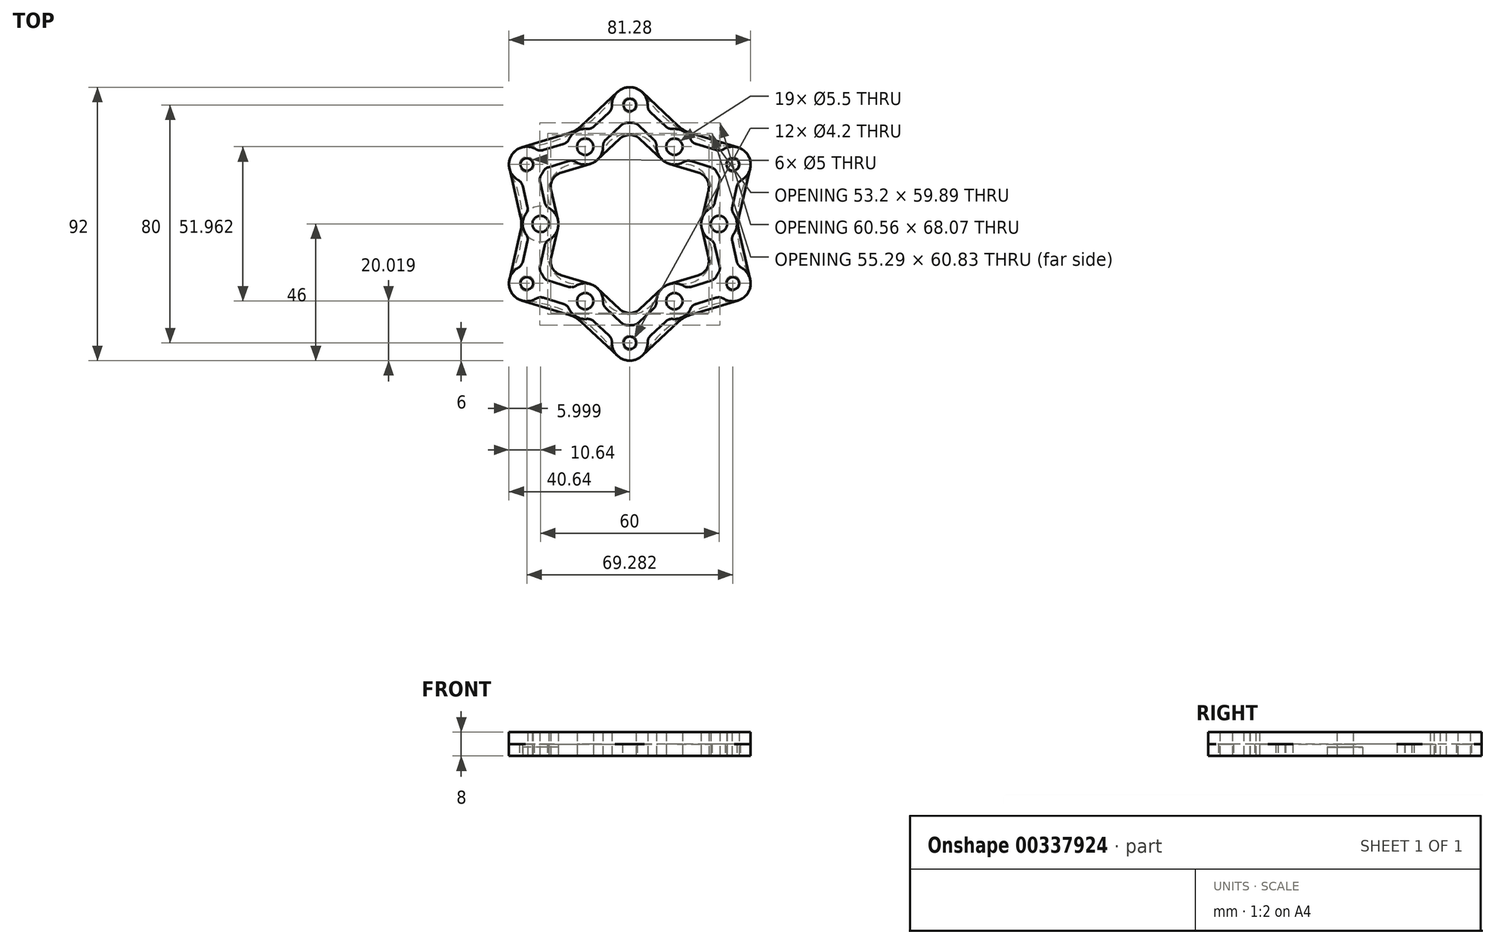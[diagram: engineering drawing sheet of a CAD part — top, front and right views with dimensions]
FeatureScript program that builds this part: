
annotation { "Feature Type Name" : "Feature", "Feature Type Description" : "" }
export const myFeature = defineFeature(function(context is Context, id is Id, definition is map)
    precondition{}
    {
        {
            var Q0;
            Q0=qCreatedBy(makeId("Top.planeOp"),FACE);
            var sketch = newSketch(context, id + "F0", { "sketchPlane" : qUnion([Q0])});
            skLineSegment(sketch, "E0", {"start": v(0, 0) * mm, "end": v(-30, 0) * mm, "construction": true});
            skLineSegment(sketch, "E1", {"start": v(0, 0) * mm, "end": v(-34.64, 20) * mm, "construction": true});
            skLineSegment(sketch, "E2", {"start": v(0, 0) * mm, "end": v(-15, 25.98) * mm, "construction": true});
            skLineSegment(sketch, "E3", {"start": v(-15, 25.98) * mm, "end": v(-12, 20.78) * mm, "construction": true});
            skLineSegment(sketch, "E4", {"start": v(0, 40) * mm, "end": v(0, 0) * mm, "construction": true});
            skCircle(sketch, "E5", {"center": v(-30, 0) * mm, "radius": 2.75 * mm, "construction": true});
            skCircle(sketch, "E6", {"center": v(-34.64, 20) * mm, "radius": 2.5 * mm});
            skCircle(sketch, "E7", {"center": v(-15, 25.98) * mm, "radius": 2.75 * mm});
            skCircle(sketch, "E8", {"center": v(0, 40) * mm, "radius": 2.5 * mm, "construction": true});
            skLineSegment(sketch, "E9", {"start": v(-30, 0) * mm, "end": v(-34.64, 20) * mm, "construction": true});
            skLineSegment(sketch, "E10", {"start": v(-15, 25.98) * mm, "end": v(-34.64, 20) * mm, "construction": true});
            skLineSegment(sketch, "E11", {"start": v(0, 40) * mm, "end": v(-15, 25.98) * mm, "construction": true});
            skArc(sketch, "E12", {"start": v(-35.08, 25.98) * mm, "mid": v(-18.03, 31.23) * mm, "end": v(-4.96, 43.37) * mm});
            skArc(sketch, "E13", {"start": v(-16, 20.07) * mm, "mid": v(-26.34, 15.2) * mm, "end": v(-25.38, 3.83) * mm});
            skLineSegment(sketch, "E14", {"start": v(-34.64, 20) * mm, "end": v(-39.84, 23) * mm, "construction": true});
            skLineSegment(sketch, "E15", {"start": v(0, 40) * mm, "end": v(0, 46) * mm, "construction": true});
            skArc(sketch, "E16", {"start": v(-39.84, 23) * mm, "mid": v(-31.45, 14.92) * mm, "end": v(-35.08, 25.98) * mm, "construction": true});
            skArc(sketch, "E17", {"start": v(-35.08, 25.98) * mm, "mid": v(-37.83, 25.08) * mm, "end": v(-39.84, 23) * mm});
            skLineSegment(sketch, "E18", {"start": v(-12, 20.78) * mm, "end": v(0, 0) * mm, "construction": true});
            skArc(sketch, "E19", {"start": v(-16, 20.07) * mm, "mid": v(-13.94, 20.08) * mm, "end": v(-12, 20.78) * mm});
            skArc(sketch, "E20", {"start": v(-12, 20.78) * mm, "mid": v(-16.06, 31.89) * mm, "end": v(-16, 20.07) * mm, "construction": true});
            skArc(sketch, "E21", {"start": v(-25.38, 3.83) * mm, "mid": v(-35.64, -2.03) * mm, "end": v(-24, 0) * mm, "construction": true});
            skArc(sketch, "E22", {"start": v(-24, 0) * mm, "mid": v(-24.36, 2.03) * mm, "end": v(-25.38, 3.83) * mm});
            skArc(sketch, "E23", {"start": v(-4.96, 43.37) * mm, "mid": v(2.8, 34.7) * mm, "end": v(0, 46) * mm, "construction": true});
            skArc(sketch, "E24", {"start": v(0, 46) * mm, "mid": v(-2.8, 45.3) * mm, "end": v(-4.96, 43.37) * mm});
            skArc(sketch, "E25.1.0", {"start": v(-40.04, -17.4) * mm, "mid": v(-40.64, -20.22) * mm, "end": v(-39.84, -23) * mm});
            skArc(sketch, "E25.1.1", {"start": v(-40.04, -17.4) * mm, "mid": v(-36.07, 0) * mm, "end": v(-40.04, 17.4) * mm});
            skCircle(sketch, "E25.1.2", {"center": v(-34.64, -20) * mm, "radius": 2.5 * mm});
            skCircle(sketch, "E25.1.3", {"center": v(-30, 0) * mm, "radius": 2.75 * mm});
            skArc(sketch, "E25.1.4", {"start": v(-12, -20.78) * mm, "mid": v(-13.94, -20.08) * mm, "end": v(-16, -20.07) * mm});
            skArc(sketch, "E25.1.5", {"start": v(-25.38, -3.83) * mm, "mid": v(-26.34, -15.2) * mm, "end": v(-16, -20.07) * mm});
            skArc(sketch, "E25.1.6", {"start": v(-25.38, -3.83) * mm, "mid": v(-24.36, -2.03) * mm, "end": v(-24, 0) * mm});
            skArc(sketch, "E25.1.7", {"start": v(-39.84, 23) * mm, "mid": v(-40.64, 20.22) * mm, "end": v(-40.04, 17.4) * mm});
            skArc(sketch, "E25.2.0", {"start": v(-4.96, -43.37) * mm, "mid": v(-2.8, -45.3) * mm, "end": v(0, -46) * mm});
            skArc(sketch, "E25.2.1", {"start": v(-4.96, -43.37) * mm, "mid": v(-18.03, -31.23) * mm, "end": v(-35.08, -25.98) * mm});
            skCircle(sketch, "E25.2.2", {"center": v(0, -40) * mm, "radius": 2.5 * mm});
            skCircle(sketch, "E25.2.3", {"center": v(-15, -25.98) * mm, "radius": 2.75 * mm});
            skArc(sketch, "E25.2.4", {"start": v(12, -20.78) * mm, "mid": v(10.42, -22.1) * mm, "end": v(9.37, -23.9) * mm});
            skArc(sketch, "E25.2.5", {"start": v(-9.37, -23.9) * mm, "mid": v(0, -30.41) * mm, "end": v(9.38, -23.9) * mm});
            skArc(sketch, "E25.2.6", {"start": v(-9.37, -23.9) * mm, "mid": v(-10.42, -22.1) * mm, "end": v(-12, -20.78) * mm});
            skArc(sketch, "E25.2.7", {"start": v(-39.84, -23) * mm, "mid": v(-37.83, -25.08) * mm, "end": v(-35.08, -25.98) * mm});
            skArc(sketch, "E25.3.0", {"start": v(35.08, -25.98) * mm, "mid": v(37.83, -25.08) * mm, "end": v(39.84, -23) * mm});
            skArc(sketch, "E25.3.1", {"start": v(35.08, -25.98) * mm, "mid": v(18.03, -31.23) * mm, "end": v(4.96, -43.37) * mm});
            skCircle(sketch, "E25.3.2", {"center": v(34.64, -20) * mm, "radius": 2.5 * mm});
            skCircle(sketch, "E25.3.3", {"center": v(15, -25.98) * mm, "radius": 2.75 * mm});
            skArc(sketch, "E25.3.4", {"start": v(24, 0) * mm, "mid": v(24.36, -2.03) * mm, "end": v(25.38, -3.83) * mm});
            skArc(sketch, "E25.3.5", {"start": v(16, -20.07) * mm, "mid": v(26.34, -15.2) * mm, "end": v(25.38, -3.83) * mm});
            skArc(sketch, "E25.3.6", {"start": v(16, -20.07) * mm, "mid": v(13.94, -20.08) * mm, "end": v(12, -20.78) * mm});
            skArc(sketch, "E25.3.7", {"start": v(0, -46) * mm, "mid": v(2.8, -45.3) * mm, "end": v(4.96, -43.37) * mm});
            skArc(sketch, "E25.4.0", {"start": v(40.04, 17.4) * mm, "mid": v(40.64, 20.22) * mm, "end": v(39.84, 23) * mm});
            skArc(sketch, "E25.4.1", {"start": v(40.04, 17.4) * mm, "mid": v(36.07, 0) * mm, "end": v(40.04, -17.4) * mm});
            skCircle(sketch, "E25.4.2", {"center": v(34.64, 20) * mm, "radius": 2.5 * mm});
            skCircle(sketch, "E25.4.3", {"center": v(30, 0) * mm, "radius": 2.75 * mm});
            skArc(sketch, "E25.4.4", {"start": v(12, 20.78) * mm, "mid": v(13.94, 20.08) * mm, "end": v(16, 20.07) * mm});
            skArc(sketch, "E25.4.5", {"start": v(25.38, 3.83) * mm, "mid": v(26.34, 15.2) * mm, "end": v(16, 20.07) * mm});
            skArc(sketch, "E25.4.6", {"start": v(25.38, 3.83) * mm, "mid": v(24.36, 2.03) * mm, "end": v(24, 0) * mm});
            skArc(sketch, "E25.4.7", {"start": v(39.84, -23) * mm, "mid": v(40.64, -20.22) * mm, "end": v(40.04, -17.4) * mm});
            skArc(sketch, "E25.5.0", {"start": v(4.96, 43.37) * mm, "mid": v(2.8, 45.3) * mm, "end": v(0, 46) * mm});
            skArc(sketch, "E25.5.1", {"start": v(4.96, 43.37) * mm, "mid": v(18.03, 31.23) * mm, "end": v(35.08, 25.98) * mm});
            skCircle(sketch, "E25.5.2", {"center": v(0, 40) * mm, "radius": 2.5 * mm});
            skCircle(sketch, "E25.5.3", {"center": v(15, 25.98) * mm, "radius": 2.75 * mm});
            skArc(sketch, "E25.5.4", {"start": v(-12, 20.78) * mm, "mid": v(-10.42, 22.1) * mm, "end": v(-9.38, 23.9) * mm});
            skArc(sketch, "E25.5.5", {"start": v(9.37, 23.9) * mm, "mid": v(0, 30.41) * mm, "end": v(-9.38, 23.9) * mm});
            skArc(sketch, "E25.5.6", {"start": v(9.37, 23.9) * mm, "mid": v(10.42, 22.1) * mm, "end": v(12, 20.78) * mm});
            skArc(sketch, "E25.5.7", {"start": v(39.84, 23) * mm, "mid": v(37.83, 25.08) * mm, "end": v(35.08, 25.98) * mm});
            skPoint(sketch, "E25.center", {"position": v(0, 0) * mm});
            skSolve(sketch);
        }
        {
            var Q0;
            Q0=makeQuery(id+"F0.imprint","IMPRINT",FACE,{"disambiguationData":[TD([[makeQuery(id+"F0.imprint","IMPRINT",EDGE,{"derivedFrom":sQuery(id+"F0.wireOp",EDGE,"E6")}),-1.0]])]});
            extrude(context, id + "F1", {"entities" : qUnion([Q0]), "depth" : 4 * mm});
        }
        {
            var Q0;
            Q0=qCreatedBy(makeId("Top.planeOp"),FACE);
            var sketch = newSketch(context, id + "F2", { "sketchPlane" : qUnion([Q0])});
            skCircle(sketch, "E26", {"center": v(-30, 0) * mm, "radius": 2.75 * mm});
            skCircle(sketch, "E27", {"center": v(-30, 0) * mm, "radius": 6 * mm});
            skSolve(sketch);
        }
        {
            var Q0;
            Q0 = qSketchRegion(id + "F2", true);
            extrude(context, id + "F3", {"entities" : qUnion([Q0]), "depth" : 3 * mm});
        }
        {
            var Q0;
            Q0=qCreatedBy(makeId("Top.planeOp"),FACE);
            var sketch = newSketch(context, id + "F4", { "sketchPlane" : qUnion([Q0])});
            skCircle(sketch, "E28", {"center": v(-30, 0) * mm, "radius": 2.75 * mm, "construction": true});
            skCircle(sketch, "E29", {"center": v(-34.64, 20) * mm, "radius": 2.1 * mm});
            skCircle(sketch, "E30", {"center": v(-15, 25.98) * mm, "radius": 2.75 * mm});
            skCircle(sketch, "E31", {"center": v(0, 40) * mm, "radius": 2.1 * mm, "construction": true});
            skLineSegment(sketch, "E32", {"start": v(-34.64, 20) * mm, "end": v(0, 0) * mm, "construction": true});
            skLineSegment(sketch, "E33", {"start": v(0, 0) * mm, "end": v(-15, 25.98) * mm, "construction": true});
            skLineSegment(sketch, "E34", {"start": v(-30, 0) * mm, "end": v(0, 0) * mm, "construction": true});
            skLineSegment(sketch, "E35", {"start": v(0, 40) * mm, "end": v(0, 0) * mm, "construction": true});
            skCircle(sketch, "E36", {"center": v(-30, 0) * mm, "radius": 6 * mm, "construction": true});
            skCircle(sketch, "E37", {"center": v(0, 40) * mm, "radius": 6 * mm, "construction": true});
            skLineSegment(sketch, "E38", {"start": v(-30, 0) * mm, "end": v(-34.64, 20) * mm, "construction": true});
            skLineSegment(sketch, "E39", {"start": v(-15, 25.98) * mm, "end": v(-34.64, 20) * mm, "construction": true});
            skLineSegment(sketch, "E40", {"start": v(0, 40) * mm, "end": v(-15, 25.98) * mm, "construction": true});
            skLineSegment(sketch, "E41", {"start": v(-35.84, -1.36) * mm, "end": v(-40.49, 18.64) * mm, "construction": true});
            skLineSegment(sketch, "E42", {"start": v(-36.39, 25.74) * mm, "end": v(-36.39, 25.74) * mm});
            skLineSegment(sketch, "E43", {"start": v(4.1, 35.62) * mm, "end": v(-10.9, 21.6) * mm, "construction": true});
            skLineSegment(sketch, "E44", {"start": v(-13.25, 20.24) * mm, "end": v(-23.06, 17.25) * mm});
            skLineSegment(sketch, "E45", {"start": v(-24.16, 1.36) * mm, "end": v(-26.47, 11.34) * mm});
            skLineSegment(sketch, "E46", {"start": v(-4.1, 44.38) * mm, "end": v(-16.38, 32.9) * mm});
            skLineSegment(sketch, "E47", {"start": v(-36.39, 25.74) * mm, "end": v(-20.3, 30.64) * mm});
            skLineSegment(sketch, "E48", {"start": v(-40.49, 18.64) * mm, "end": v(-40.49, 18.64) * mm});
            skArc(sketch, "E49", {"start": v(-28.8, 21.36) * mm, "mid": v(-31.64, 25.2) * mm, "end": v(-36.39, 25.74) * mm, "construction": true});
            skArc(sketch, "E50", {"start": v(-36.39, 25.74) * mm, "mid": v(-39.84, 23) * mm, "end": v(-40.49, 18.64) * mm});
            skArc(sketch, "E51", {"start": v(-32.9, 14.26) * mm, "mid": v(-29.44, 17) * mm, "end": v(-28.8, 21.36) * mm, "construction": true});
            skArc(sketch, "E52", {"start": v(-40.49, 18.64) * mm, "mid": v(-37.64, 14.8) * mm, "end": v(-32.9, 14.26) * mm, "construction": true});
            skLineSegment(sketch, "E53", {"start": v(-27.53, 15.9) * mm, "end": v(-28.8, 21.36) * mm, "construction": true});
            skLineSegment(sketch, "E54", {"start": v(-27.53, 15.9) * mm, "end": v(-32.9, 14.26) * mm, "construction": true});
            skArc(sketch, "E55", {"start": v(-13.25, 20.24) * mm, "mid": v(-12, 20.78) * mm, "end": v(-10.9, 21.6) * mm});
            skArc(sketch, "E56", {"start": v(-10.9, 21.6) * mm, "mid": v(-18, 31.18) * mm, "end": v(-13.25, 20.24) * mm, "construction": true});
            skLineSegment(sketch, "E57", {"start": v(-18.08, 31.31) * mm, "end": v(-16.75, 31.72) * mm, "construction": true});
            skLineSegment(sketch, "E58", {"start": v(-18.08, 31.31) * mm, "end": v(-19.1, 30.36) * mm, "construction": true});
            skPoint(sketch, "E59.visualSharp", {"position": v(-18.08, 31.31) * mm});
            skArc(sketch, "E59.filletArc", {"start": v(-20.3, 30.64) * mm, "mid": v(-18.21, 31.55) * mm, "end": v(-16.38, 32.9) * mm});
            skPoint(sketch, "E60.visualSharp", {"position": v(-27.53, 15.9) * mm});
            skArc(sketch, "E60.filletArc", {"start": v(-23.06, 17.25) * mm, "mid": v(-25.93, 14.97) * mm, "end": v(-26.47, 11.34) * mm});
            skArc(sketch, "E61.1.0", {"start": v(-40.49, -18.64) * mm, "mid": v(-39.84, -23) * mm, "end": v(-36.39, -25.74) * mm});
            skLineSegment(sketch, "E61.1.1", {"start": v(-40.49, -18.64) * mm, "end": v(-36.68, -2.26) * mm});
            skArc(sketch, "E61.1.2", {"start": v(-36.68, -2.26) * mm, "mid": v(-36.43, 0) * mm, "end": v(-36.68, 2.26) * mm});
            skLineSegment(sketch, "E61.1.3", {"start": v(-40.49, 18.64) * mm, "end": v(-36.68, 2.26) * mm});
            skArc(sketch, "E61.1.4", {"start": v(-24.16, -1.36) * mm, "mid": v(-24, 0) * mm, "end": v(-24.16, 1.36) * mm});
            skLineSegment(sketch, "E61.1.5", {"start": v(-24.16, -1.36) * mm, "end": v(-26.47, -11.34) * mm});
            skArc(sketch, "E61.1.6", {"start": v(-26.47, -11.34) * mm, "mid": v(-25.93, -14.97) * mm, "end": v(-23.06, -17.25) * mm});
            skLineSegment(sketch, "E61.1.7", {"start": v(-13.25, -20.24) * mm, "end": v(-23.06, -17.25) * mm});
            skArc(sketch, "E61.2.0", {"start": v(-4.1, -44.38) * mm, "mid": v(0, -46) * mm, "end": v(4.1, -44.38) * mm});
            skLineSegment(sketch, "E61.2.1", {"start": v(-4.1, -44.38) * mm, "end": v(-16.38, -32.9) * mm});
            skArc(sketch, "E61.2.2", {"start": v(-16.38, -32.9) * mm, "mid": v(-18.21, -31.55) * mm, "end": v(-20.3, -30.64) * mm});
            skLineSegment(sketch, "E61.2.3", {"start": v(-36.39, -25.74) * mm, "end": v(-20.3, -30.64) * mm});
            skArc(sketch, "E61.2.4", {"start": v(-10.9, -21.6) * mm, "mid": v(-12, -20.78) * mm, "end": v(-13.25, -20.24) * mm});
            skLineSegment(sketch, "E61.2.5", {"start": v(-10.9, -21.6) * mm, "end": v(-3.41, -28.6) * mm});
            skArc(sketch, "E61.2.6", {"start": v(-3.41, -28.6) * mm, "mid": v(0, -29.94) * mm, "end": v(3.41, -28.6) * mm});
            skLineSegment(sketch, "E61.2.7", {"start": v(10.9, -21.6) * mm, "end": v(3.41, -28.6) * mm});
            skArc(sketch, "E61.3.0", {"start": v(36.39, -25.74) * mm, "mid": v(39.84, -23) * mm, "end": v(40.49, -18.64) * mm});
            skLineSegment(sketch, "E61.3.1", {"start": v(36.39, -25.74) * mm, "end": v(20.3, -30.64) * mm});
            skArc(sketch, "E61.3.2", {"start": v(20.3, -30.64) * mm, "mid": v(18.21, -31.55) * mm, "end": v(16.38, -32.9) * mm});
            skLineSegment(sketch, "E61.3.3", {"start": v(4.1, -44.38) * mm, "end": v(16.38, -32.9) * mm});
            skArc(sketch, "E61.3.4", {"start": v(13.25, -20.24) * mm, "mid": v(12, -20.78) * mm, "end": v(10.9, -21.6) * mm});
            skLineSegment(sketch, "E61.3.5", {"start": v(13.25, -20.24) * mm, "end": v(23.06, -17.25) * mm});
            skArc(sketch, "E61.3.6", {"start": v(23.06, -17.25) * mm, "mid": v(25.93, -14.97) * mm, "end": v(26.47, -11.34) * mm});
            skLineSegment(sketch, "E61.3.7", {"start": v(24.16, -1.36) * mm, "end": v(26.47, -11.34) * mm});
            skArc(sketch, "E61.4.0", {"start": v(40.49, 18.64) * mm, "mid": v(39.84, 23) * mm, "end": v(36.39, 25.74) * mm});
            skLineSegment(sketch, "E61.4.1", {"start": v(40.49, 18.64) * mm, "end": v(36.68, 2.26) * mm});
            skArc(sketch, "E61.4.2", {"start": v(36.68, 2.26) * mm, "mid": v(36.43, 0) * mm, "end": v(36.68, -2.26) * mm});
            skLineSegment(sketch, "E61.4.3", {"start": v(40.49, -18.64) * mm, "end": v(36.68, -2.26) * mm});
            skArc(sketch, "E61.4.4", {"start": v(24.16, 1.36) * mm, "mid": v(24, 0) * mm, "end": v(24.16, -1.36) * mm});
            skLineSegment(sketch, "E61.4.5", {"start": v(24.16, 1.36) * mm, "end": v(26.47, 11.34) * mm});
            skArc(sketch, "E61.4.6", {"start": v(26.47, 11.34) * mm, "mid": v(25.93, 14.97) * mm, "end": v(23.06, 17.25) * mm});
            skLineSegment(sketch, "E61.4.7", {"start": v(13.25, 20.24) * mm, "end": v(23.06, 17.25) * mm});
            skArc(sketch, "E61.5.0", {"start": v(4.1, 44.38) * mm, "mid": v(0, 46) * mm, "end": v(-4.1, 44.38) * mm});
            skLineSegment(sketch, "E61.5.1", {"start": v(4.1, 44.38) * mm, "end": v(16.38, 32.9) * mm});
            skArc(sketch, "E61.5.2", {"start": v(16.38, 32.9) * mm, "mid": v(18.21, 31.55) * mm, "end": v(20.3, 30.64) * mm});
            skLineSegment(sketch, "E61.5.3", {"start": v(36.39, 25.74) * mm, "end": v(20.3, 30.64) * mm});
            skArc(sketch, "E61.5.4", {"start": v(10.9, 21.6) * mm, "mid": v(12, 20.78) * mm, "end": v(13.25, 20.24) * mm});
            skLineSegment(sketch, "E61.5.5", {"start": v(10.9, 21.6) * mm, "end": v(3.41, 28.6) * mm});
            skArc(sketch, "E61.5.6", {"start": v(3.41, 28.6) * mm, "mid": v(0, 29.94) * mm, "end": v(-3.41, 28.6) * mm});
            skLineSegment(sketch, "E61.5.7", {"start": v(-10.9, 21.6) * mm, "end": v(-3.41, 28.6) * mm});
            skPoint(sketch, "E61.center", {"position": v(0, 0) * mm});
            skCircle(sketch, "E62.1.0", {"center": v(-34.64, -20) * mm, "radius": 2.1 * mm});
            skCircle(sketch, "E62.1.1", {"center": v(-30, 0) * mm, "radius": 2.75 * mm});
            skCircle(sketch, "E62.2.0", {"center": v(0, -40) * mm, "radius": 2.1 * mm});
            skCircle(sketch, "E62.2.1", {"center": v(-15, -25.98) * mm, "radius": 2.75 * mm});
            skCircle(sketch, "E62.3.0", {"center": v(34.64, -20) * mm, "radius": 2.1 * mm});
            skCircle(sketch, "E62.3.1", {"center": v(15, -25.98) * mm, "radius": 2.75 * mm});
            skCircle(sketch, "E62.4.0", {"center": v(34.64, 20) * mm, "radius": 2.1 * mm});
            skCircle(sketch, "E62.4.1", {"center": v(30, 0) * mm, "radius": 2.75 * mm});
            skCircle(sketch, "E62.5.0", {"center": v(0, 40) * mm, "radius": 2.1 * mm});
            skCircle(sketch, "E62.5.1", {"center": v(15, 25.98) * mm, "radius": 2.75 * mm});
            skSolve(sketch);
        }
        {
            var Q0;
            Q0=makeQuery(id+"F4.imprint","IMPRINT",FACE,{"disambiguationData":[TD([[makeQuery(id+"F4.imprint","IMPRINT",EDGE,{"derivedFrom":sQuery(id+"F4.wireOp",EDGE,"E29")}),-1.0]])]});
            extrude(context, id + "F5", {"entities" : qUnion([Q0]), "depth" : 8 * mm});
        }
        {
            var Q0;
            Q0=qCreatedBy(makeId("Top.planeOp"),FACE);
            var sketch = newSketch(context, id + "F6", { "sketchPlane" : qUnion([Q0])});
            skLineSegment(sketch, "E63", {"start": v(-30, 0) * mm, "end": v(0, 0) * mm, "construction": true});
            skLineSegment(sketch, "E64", {"start": v(0, 0) * mm, "end": v(-34.64, 20) * mm, "construction": true});
            skLineSegment(sketch, "E65", {"start": v(-15, 25.98) * mm, "end": v(0, 0) * mm, "construction": true});
            skLineSegment(sketch, "E66", {"start": v(0, 40) * mm, "end": v(0, 0) * mm, "construction": true});
            skCircle(sketch, "E67", {"center": v(-30, 0) * mm, "radius": 2.75 * mm, "construction": true});
            skCircle(sketch, "E68", {"center": v(-15, 25.98) * mm, "radius": 2.75 * mm});
            skCircle(sketch, "E69", {"center": v(-34.64, 20) * mm, "radius": 2.1 * mm});
            skCircle(sketch, "E70", {"center": v(0, 40) * mm, "radius": 2.1 * mm, "construction": true});
            skLineSegment(sketch, "E71", {"start": v(-34.64, 20) * mm, "end": v(-30, 0) * mm, "construction": true});
            skLineSegment(sketch, "E72", {"start": v(-34.64, 20) * mm, "end": v(-15, 25.98) * mm, "construction": true});
            skLineSegment(sketch, "E73", {"start": v(0, 40) * mm, "end": v(-15, 25.98) * mm, "construction": true});
            skLineSegment(sketch, "E74", {"start": v(-6.95, 37.61) * mm, "end": v(-12.15, 32.75) * mm});
            skLineSegment(sketch, "E75", {"start": v(-36.05, 12.79) * mm, "end": v(-34.1, 4.38) * mm, "construction": true});
            skLineSegment(sketch, "E76", {"start": v(-28.25, 5.74) * mm, "end": v(-30.2, 14.14) * mm, "construction": true});
            skLineSegment(sketch, "E77", {"start": v(-27.35, 19.08) * mm, "end": v(-20.54, 21.16) * mm});
            skLineSegment(sketch, "E78", {"start": v(-8.05, 28.37) * mm, "end": v(-2.85, 33.23) * mm});
            skLineSegment(sketch, "E79", {"start": v(-29.1, 24.82) * mm, "end": v(-22.3, 26.9) * mm});
            skArc(sketch, "E80", {"start": v(-36.39, 14.26) * mm, "mid": v(-33.28, 14.16) * mm, "end": v(-30.54, 15.62) * mm, "construction": true});
            skArc(sketch, "E81", {"start": v(-31.53, 25.13) * mm, "mid": v(-39.84, 23) * mm, "end": v(-37.53, 14.74) * mm});
            skArc(sketch, "E82", {"start": v(-28.8, 18.64) * mm, "mid": v(-28.9, 21.75) * mm, "end": v(-30.54, 24.38) * mm, "construction": true});
            skArc(sketch, "E83", {"start": v(-29.73, 16.55) * mm, "mid": v(-29.44, 17) * mm, "end": v(-29.2, 17.48) * mm});
            skArc(sketch, "E84", {"start": v(-20.84, 27.34) * mm, "mid": v(-20.74, 24.23) * mm, "end": v(-19.1, 21.6) * mm, "construction": true});
            skArc(sketch, "E85", {"start": v(-14.46, 31.96) * mm, "mid": v(-18, 31.18) * mm, "end": v(-20.44, 28.5) * mm});
            skArc(sketch, "E86", {"start": v(-9.16, 27.34) * mm, "mid": v(-10.62, 30.08) * mm, "end": v(-13.25, 31.72) * mm, "construction": true});
            skArc(sketch, "E87", {"start": v(-18.11, 20.85) * mm, "mid": v(-12, 20.78) * mm, "end": v(-9, 26.11) * mm});
            skArc(sketch, "E88", {"start": v(-5.84, 38.64) * mm, "mid": v(-4.38, 35.9) * mm, "end": v(-1.75, 34.26) * mm, "construction": true});
            skArc(sketch, "E89", {"start": v(-0.54, 34.02) * mm, "mid": v(4.38, 44.1) * mm, "end": v(-6, 39.87) * mm, "construction": true});
            skArc(sketch, "E90", {"start": v(-34.1, 4.38) * mm, "mid": v(-28.64, -5.84) * mm, "end": v(-28.25, 5.74) * mm, "construction": true});
            skArc(sketch, "E91", {"start": v(-28.25, 5.74) * mm, "mid": v(-31.36, 5.84) * mm, "end": v(-34.1, 4.38) * mm, "construction": true});
            skPoint(sketch, "E92.visualSharp", {"position": v(-36.39, 14.26) * mm});
            skArc(sketch, "E92.filletArc", {"start": v(-36.05, 12.79) * mm, "mid": v(-36.58, 13.92) * mm, "end": v(-37.53, 14.74) * mm, "construction": true});
            skPoint(sketch, "E93.visualSharp", {"position": v(-30.54, 24.38) * mm});
            skArc(sketch, "E93.filletArc", {"start": v(-31.53, 25.13) * mm, "mid": v(-30.35, 24.72) * mm, "end": v(-29.1, 24.82) * mm});
            skPoint(sketch, "E94.visualSharp", {"position": v(-20.84, 27.34) * mm});
            skArc(sketch, "E94.filletArc", {"start": v(-22.3, 26.9) * mm, "mid": v(-21.2, 27.5) * mm, "end": v(-20.44, 28.5) * mm});
            skPoint(sketch, "E95.visualSharp", {"position": v(-13.25, 31.72) * mm});
            skArc(sketch, "E95.filletArc", {"start": v(-14.46, 31.96) * mm, "mid": v(-13.22, 32.1) * mm, "end": v(-12.15, 32.75) * mm});
            skPoint(sketch, "E96.visualSharp", {"position": v(-5.84, 38.64) * mm});
            skArc(sketch, "E96.filletArc", {"start": v(-6.95, 37.61) * mm, "mid": v(-6.23, 38.64) * mm, "end": v(-6, 39.87) * mm});
            skPoint(sketch, "E97.visualSharp", {"position": v(-1.75, 34.26) * mm});
            skArc(sketch, "E97.filletArc", {"start": v(-0.54, 34.02) * mm, "mid": v(-1.78, 33.87) * mm, "end": v(-2.85, 33.23) * mm});
            skPoint(sketch, "E98.visualSharp", {"position": v(-9.16, 27.34) * mm});
            skArc(sketch, "E98.filletArc", {"start": v(-8.05, 28.37) * mm, "mid": v(-8.77, 27.34) * mm, "end": v(-9, 26.11) * mm});
            skPoint(sketch, "E99.visualSharp", {"position": v(-19.1, 21.6) * mm});
            skArc(sketch, "E99.filletArc", {"start": v(-18.11, 20.85) * mm, "mid": v(-19.3, 21.26) * mm, "end": v(-20.54, 21.16) * mm});
            skPoint(sketch, "E100.visualSharp", {"position": v(-28.8, 18.64) * mm});
            skArc(sketch, "E100.filletArc", {"start": v(-27.35, 19.08) * mm, "mid": v(-28.45, 18.48) * mm, "end": v(-29.2, 17.48) * mm});
            skPoint(sketch, "E101.visualSharp", {"position": v(-30.54, 15.62) * mm});
            skArc(sketch, "E101.filletArc", {"start": v(-29.73, 16.55) * mm, "mid": v(-30.22, 15.4) * mm, "end": v(-30.2, 14.14) * mm, "construction": true});
            skArc(sketch, "E102.1.0", {"start": v(-29.2, -17.48) * mm, "mid": v(-29.44, -17) * mm, "end": v(-29.73, -16.55) * mm});
            skArc(sketch, "E102.1.1", {"start": v(-30.2, -14.14) * mm, "mid": v(-30.22, -15.4) * mm, "end": v(-29.73, -16.55) * mm});
            skLineSegment(sketch, "E102.1.2", {"start": v(-30.2, -14.14) * mm, "end": v(-28.6, -7.21) * mm});
            skArc(sketch, "E102.1.3", {"start": v(-27.11, -5.26) * mm, "mid": v(-28.06, -6.08) * mm, "end": v(-28.6, -7.21) * mm});
            skArc(sketch, "E102.1.4", {"start": v(-27.11, -5.26) * mm, "mid": v(-24, 0) * mm, "end": v(-27.11, 5.26) * mm});
            skArc(sketch, "E102.1.5", {"start": v(-28.6, 7.21) * mm, "mid": v(-28.06, 6.08) * mm, "end": v(-27.11, 5.26) * mm});
            skLineSegment(sketch, "E102.1.6", {"start": v(-28.6, 7.21) * mm, "end": v(-30.2, 14.14) * mm});
            skArc(sketch, "E102.1.7", {"start": v(-29.73, 16.55) * mm, "mid": v(-30.22, 15.4) * mm, "end": v(-30.2, 14.14) * mm});
            skArc(sketch, "E102.1.8", {"start": v(-36.05, 12.79) * mm, "mid": v(-36.58, 13.92) * mm, "end": v(-37.53, 14.74) * mm});
            skLineSegment(sketch, "E102.1.9", {"start": v(-36.05, 12.79) * mm, "end": v(-34.44, 5.86) * mm});
            skArc(sketch, "E102.1.10", {"start": v(-34.9, 3.45) * mm, "mid": v(-34.42, 4.6) * mm, "end": v(-34.44, 5.86) * mm});
            skArc(sketch, "E102.1.11", {"start": v(-34.9, 3.45) * mm, "mid": v(-36, 0) * mm, "end": v(-34.9, -3.45) * mm});
            skArc(sketch, "E102.1.12", {"start": v(-34.44, -5.86) * mm, "mid": v(-34.42, -4.6) * mm, "end": v(-34.9, -3.45) * mm});
            skLineSegment(sketch, "E102.1.13", {"start": v(-36.05, -12.79) * mm, "end": v(-34.44, -5.86) * mm});
            skArc(sketch, "E102.1.14", {"start": v(-37.53, -14.74) * mm, "mid": v(-36.58, -13.92) * mm, "end": v(-36.05, -12.79) * mm});
            skArc(sketch, "E102.1.15", {"start": v(-37.53, -14.74) * mm, "mid": v(-39.84, -23) * mm, "end": v(-31.53, -25.13) * mm});
            skCircle(sketch, "E102.1.16", {"center": v(-34.64, -20) * mm, "radius": 2.1 * mm});
            skCircle(sketch, "E102.1.17", {"center": v(-30, 0) * mm, "radius": 2.75 * mm});
            skArc(sketch, "E102.2.0", {"start": v(0.54, -34.02) * mm, "mid": v(0, -34) * mm, "end": v(-0.54, -34.02) * mm});
            skArc(sketch, "E102.2.1", {"start": v(-2.85, -33.23) * mm, "mid": v(-1.78, -33.87) * mm, "end": v(-0.54, -34.02) * mm});
            skLineSegment(sketch, "E102.2.2", {"start": v(-2.85, -33.23) * mm, "end": v(-8.05, -28.37) * mm});
            skArc(sketch, "E102.2.3", {"start": v(-9, -26.11) * mm, "mid": v(-8.77, -27.34) * mm, "end": v(-8.05, -28.37) * mm});
            skArc(sketch, "E102.2.4", {"start": v(-9, -26.11) * mm, "mid": v(-12, -20.78) * mm, "end": v(-18.11, -20.85) * mm});
            skArc(sketch, "E102.2.5", {"start": v(-20.54, -21.16) * mm, "mid": v(-19.3, -21.26) * mm, "end": v(-18.11, -20.85) * mm});
            skLineSegment(sketch, "E102.2.6", {"start": v(-20.54, -21.16) * mm, "end": v(-27.35, -19.08) * mm});
            skArc(sketch, "E102.2.7", {"start": v(-29.2, -17.48) * mm, "mid": v(-28.45, -18.48) * mm, "end": v(-27.35, -19.08) * mm});
            skArc(sketch, "E102.2.8", {"start": v(-29.1, -24.82) * mm, "mid": v(-30.35, -24.72) * mm, "end": v(-31.53, -25.13) * mm});
            skLineSegment(sketch, "E102.2.9", {"start": v(-29.1, -24.82) * mm, "end": v(-22.3, -26.9) * mm});
            skArc(sketch, "E102.2.10", {"start": v(-20.44, -28.5) * mm, "mid": v(-21.2, -27.5) * mm, "end": v(-22.3, -26.9) * mm});
            skArc(sketch, "E102.2.11", {"start": v(-20.44, -28.5) * mm, "mid": v(-18, -31.18) * mm, "end": v(-14.46, -31.96) * mm});
            skArc(sketch, "E102.2.12", {"start": v(-12.15, -32.75) * mm, "mid": v(-13.22, -32.1) * mm, "end": v(-14.46, -31.96) * mm});
            skLineSegment(sketch, "E102.2.13", {"start": v(-6.95, -37.61) * mm, "end": v(-12.15, -32.75) * mm});
            skArc(sketch, "E102.2.14", {"start": v(-6, -39.87) * mm, "mid": v(-6.23, -38.64) * mm, "end": v(-6.95, -37.61) * mm});
            skArc(sketch, "E102.2.15", {"start": v(-6, -39.87) * mm, "mid": v(0, -46) * mm, "end": v(6, -39.87) * mm});
            skCircle(sketch, "E102.2.16", {"center": v(0, -40) * mm, "radius": 2.1 * mm});
            skCircle(sketch, "E102.2.17", {"center": v(-15, -25.98) * mm, "radius": 2.75 * mm});
            skArc(sketch, "E102.3.0", {"start": v(29.73, -16.55) * mm, "mid": v(29.44, -17) * mm, "end": v(29.2, -17.48) * mm});
            skArc(sketch, "E102.3.1", {"start": v(27.35, -19.08) * mm, "mid": v(28.45, -18.48) * mm, "end": v(29.2, -17.48) * mm});
            skLineSegment(sketch, "E102.3.2", {"start": v(27.35, -19.08) * mm, "end": v(20.54, -21.16) * mm});
            skArc(sketch, "E102.3.3", {"start": v(18.11, -20.85) * mm, "mid": v(19.3, -21.26) * mm, "end": v(20.54, -21.16) * mm});
            skArc(sketch, "E102.3.4", {"start": v(18.11, -20.85) * mm, "mid": v(12, -20.78) * mm, "end": v(9, -26.11) * mm});
            skArc(sketch, "E102.3.5", {"start": v(8.05, -28.37) * mm, "mid": v(8.77, -27.34) * mm, "end": v(9, -26.11) * mm});
            skLineSegment(sketch, "E102.3.6", {"start": v(8.05, -28.37) * mm, "end": v(2.85, -33.23) * mm});
            skArc(sketch, "E102.3.7", {"start": v(0.54, -34.02) * mm, "mid": v(1.78, -33.87) * mm, "end": v(2.85, -33.23) * mm});
            skArc(sketch, "E102.3.8", {"start": v(6.95, -37.61) * mm, "mid": v(6.23, -38.64) * mm, "end": v(6, -39.87) * mm});
            skLineSegment(sketch, "E102.3.9", {"start": v(6.95, -37.61) * mm, "end": v(12.15, -32.75) * mm});
            skArc(sketch, "E102.3.10", {"start": v(14.46, -31.96) * mm, "mid": v(13.22, -32.1) * mm, "end": v(12.15, -32.75) * mm});
            skArc(sketch, "E102.3.11", {"start": v(14.46, -31.96) * mm, "mid": v(18, -31.18) * mm, "end": v(20.44, -28.5) * mm});
            skArc(sketch, "E102.3.12", {"start": v(22.3, -26.9) * mm, "mid": v(21.2, -27.5) * mm, "end": v(20.44, -28.5) * mm});
            skLineSegment(sketch, "E102.3.13", {"start": v(29.1, -24.82) * mm, "end": v(22.3, -26.9) * mm});
            skArc(sketch, "E102.3.14", {"start": v(31.53, -25.13) * mm, "mid": v(30.35, -24.72) * mm, "end": v(29.1, -24.82) * mm});
            skArc(sketch, "E102.3.15", {"start": v(31.53, -25.13) * mm, "mid": v(39.84, -23) * mm, "end": v(37.53, -14.74) * mm});
            skCircle(sketch, "E102.3.16", {"center": v(34.64, -20) * mm, "radius": 2.1 * mm});
            skCircle(sketch, "E102.3.17", {"center": v(15, -25.98) * mm, "radius": 2.75 * mm});
            skArc(sketch, "E102.4.0", {"start": v(29.2, 17.48) * mm, "mid": v(29.44, 17) * mm, "end": v(29.73, 16.55) * mm});
            skArc(sketch, "E102.4.1", {"start": v(30.2, 14.14) * mm, "mid": v(30.22, 15.4) * mm, "end": v(29.73, 16.55) * mm});
            skLineSegment(sketch, "E102.4.2", {"start": v(30.2, 14.14) * mm, "end": v(28.6, 7.21) * mm});
            skArc(sketch, "E102.4.3", {"start": v(27.11, 5.26) * mm, "mid": v(28.06, 6.08) * mm, "end": v(28.6, 7.21) * mm});
            skArc(sketch, "E102.4.4", {"start": v(27.11, 5.26) * mm, "mid": v(24, 0) * mm, "end": v(27.11, -5.26) * mm});
            skArc(sketch, "E102.4.5", {"start": v(28.6, -7.21) * mm, "mid": v(28.06, -6.08) * mm, "end": v(27.11, -5.26) * mm});
            skLineSegment(sketch, "E102.4.6", {"start": v(28.6, -7.21) * mm, "end": v(30.2, -14.14) * mm});
            skArc(sketch, "E102.4.7", {"start": v(29.73, -16.55) * mm, "mid": v(30.22, -15.4) * mm, "end": v(30.2, -14.14) * mm});
            skArc(sketch, "E102.4.8", {"start": v(36.05, -12.79) * mm, "mid": v(36.58, -13.92) * mm, "end": v(37.53, -14.74) * mm});
            skLineSegment(sketch, "E102.4.9", {"start": v(36.05, -12.79) * mm, "end": v(34.44, -5.86) * mm});
            skArc(sketch, "E102.4.10", {"start": v(34.9, -3.45) * mm, "mid": v(34.42, -4.6) * mm, "end": v(34.44, -5.86) * mm});
            skArc(sketch, "E102.4.11", {"start": v(34.9, -3.45) * mm, "mid": v(36, 0) * mm, "end": v(34.9, 3.45) * mm});
            skArc(sketch, "E102.4.12", {"start": v(34.44, 5.86) * mm, "mid": v(34.42, 4.6) * mm, "end": v(34.9, 3.45) * mm});
            skLineSegment(sketch, "E102.4.13", {"start": v(36.05, 12.79) * mm, "end": v(34.44, 5.86) * mm});
            skArc(sketch, "E102.4.14", {"start": v(37.53, 14.74) * mm, "mid": v(36.58, 13.92) * mm, "end": v(36.05, 12.79) * mm});
            skArc(sketch, "E102.4.15", {"start": v(37.53, 14.74) * mm, "mid": v(39.84, 23) * mm, "end": v(31.53, 25.13) * mm});
            skCircle(sketch, "E102.4.16", {"center": v(34.64, 20) * mm, "radius": 2.1 * mm});
            skCircle(sketch, "E102.4.17", {"center": v(30, 0) * mm, "radius": 2.75 * mm});
            skArc(sketch, "E102.5.0", {"start": v(-0.54, 34.02) * mm, "mid": v(0, 34) * mm, "end": v(0.54, 34.02) * mm});
            skArc(sketch, "E102.5.1", {"start": v(2.85, 33.23) * mm, "mid": v(1.78, 33.87) * mm, "end": v(0.54, 34.02) * mm});
            skLineSegment(sketch, "E102.5.2", {"start": v(2.85, 33.23) * mm, "end": v(8.05, 28.37) * mm});
            skArc(sketch, "E102.5.3", {"start": v(9, 26.11) * mm, "mid": v(8.77, 27.34) * mm, "end": v(8.05, 28.37) * mm});
            skArc(sketch, "E102.5.4", {"start": v(9, 26.11) * mm, "mid": v(12, 20.78) * mm, "end": v(18.11, 20.85) * mm});
            skArc(sketch, "E102.5.5", {"start": v(20.54, 21.16) * mm, "mid": v(19.3, 21.26) * mm, "end": v(18.11, 20.85) * mm});
            skLineSegment(sketch, "E102.5.6", {"start": v(20.54, 21.16) * mm, "end": v(27.35, 19.08) * mm});
            skArc(sketch, "E102.5.7", {"start": v(29.2, 17.48) * mm, "mid": v(28.45, 18.48) * mm, "end": v(27.35, 19.08) * mm});
            skArc(sketch, "E102.5.8", {"start": v(29.1, 24.82) * mm, "mid": v(30.35, 24.72) * mm, "end": v(31.53, 25.13) * mm});
            skLineSegment(sketch, "E102.5.9", {"start": v(29.1, 24.82) * mm, "end": v(22.3, 26.9) * mm});
            skArc(sketch, "E102.5.10", {"start": v(20.44, 28.5) * mm, "mid": v(21.2, 27.5) * mm, "end": v(22.3, 26.9) * mm});
            skArc(sketch, "E102.5.11", {"start": v(20.44, 28.5) * mm, "mid": v(18, 31.18) * mm, "end": v(14.46, 31.96) * mm});
            skArc(sketch, "E102.5.12", {"start": v(12.15, 32.75) * mm, "mid": v(13.22, 32.1) * mm, "end": v(14.46, 31.96) * mm});
            skLineSegment(sketch, "E102.5.13", {"start": v(6.95, 37.61) * mm, "end": v(12.15, 32.75) * mm});
            skArc(sketch, "E102.5.14", {"start": v(6, 39.87) * mm, "mid": v(6.23, 38.64) * mm, "end": v(6.95, 37.61) * mm});
            skArc(sketch, "E102.5.15", {"start": v(6, 39.87) * mm, "mid": v(0, 46) * mm, "end": v(-6, 39.87) * mm});
            skCircle(sketch, "E102.5.16", {"center": v(0, 40) * mm, "radius": 2.1 * mm});
            skCircle(sketch, "E102.5.17", {"center": v(15, 25.98) * mm, "radius": 2.75 * mm});
            skPoint(sketch, "E102.center", {"position": v(0, 0) * mm});
            skSolve(sketch);
        }
        {
            var Q0;
            Q0 = qSketchRegion(id + "F6", true);
            extrude(context, id + "F7", {"entities" : qUnion([Q0]), "depth" : 8 * mm});
        }
    });
